# Revit family: U Series Nozzles
name_source: partatom
category: Conexões de tubo
units: mm (PartAtom-declared; Revit-internal decimal feet)

## family parameters
Com base no plano de trabalho = Sim
Compartilhado = Não
Corte com vazios quando carregada = Não
Cota do conector redondo = Utilizar diâmetro
Número OmniClass = 23.60.30.11.14
Sempre na vertical = Sim
Tipo de parte = Cobertura
Título OmniClass = Pipework Fittings

## types (4) — shared parameters
Angle = 20.00°
DT1 = 0 ft
DT12 = 0 ft
DT13 = 0 ft
DT2 = 0 ft
DT6 = 0 ft
Descrição = Spray Nozzles U Series
Elevação-padrão = 4 ft
H2 = 1 ft
Metal = PARAFUSO
Plastic 2 = Black Plastic
RainBird: Product Link = https://store.rainbird.com
Reviw = R01
SupportProjetos: Level of Detail = LOD 300
SupportProjetos: Reviw Date = 26/03/2021
Water = Water
Water Visibility (Circle) = Sim

## per-type parameters (varying)
| type | Blue Plastic | Modelo | Plastic 1 | Type | URL |
| U8 Series | Transparent Plastic | U8 | Green | 1 ft |  |
| U10 Series | Blue Plastic | U10 | Blue Plastic | 2 ft |  |
| U12 Series | Transparent Plastic | U12 | Brown | 3 ft | https://www.rainbird.com |
| U15 Series | Transparent Plastic | U15 | Black | 4 ft |  |
